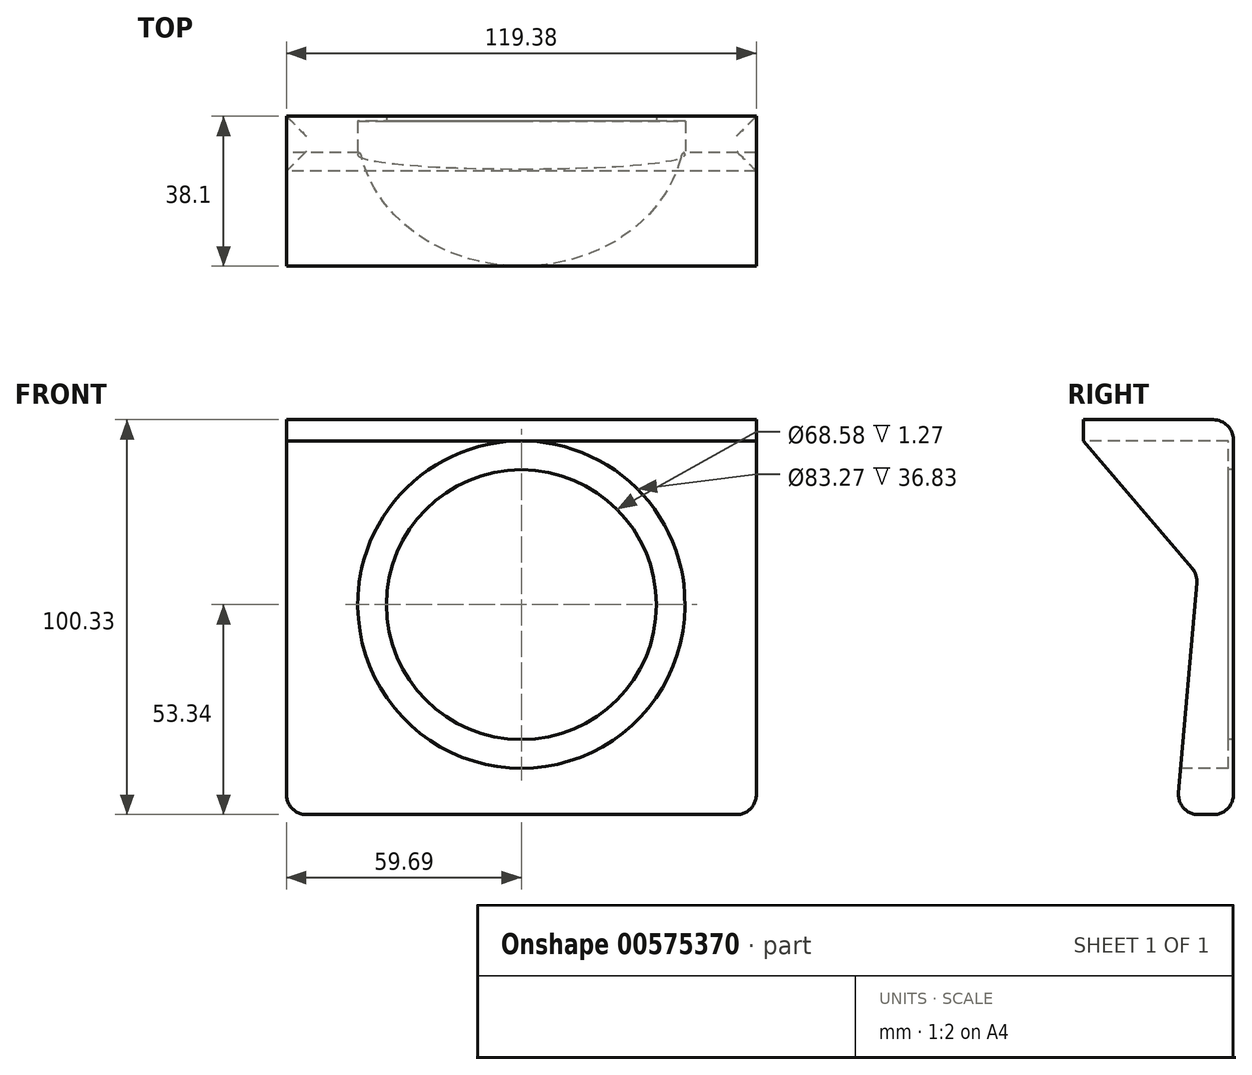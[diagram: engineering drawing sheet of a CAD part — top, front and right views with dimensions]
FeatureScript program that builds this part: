
annotation { "Feature Type Name" : "Feature", "Feature Type Description" : "" }
export const myFeature = defineFeature(function(context is Context, id is Id, definition is map)
    precondition{}
    {
        {
            var Q0;
            Q0=qCreatedBy(makeId("Front.planeOp"),FACE);
            var sketch = newSketch(context, id + "F0", { "sketchPlane" : qUnion([Q0])});
            skCircle(sketch, "E0", {"center": v(0, 0) * mm, "radius": 34.3 * mm});
            skLineSegment(sketch, "E1", {"start": v(-59.7, 47) * mm, "end": v(59.69, 47) * mm});
            skLineSegment(sketch, "E2", {"start": v(-59.7, 47) * mm, "end": v(-59.7, -53.34) * mm});
            skLineSegment(sketch, "E3", {"start": v(59.69, 47) * mm, "end": v(59.7, -53.34) * mm});
            skLineSegment(sketch, "E4", {"start": v(59.7, -53.34) * mm, "end": v(-59.7, -53.34) * mm});
            skSolve(sketch);
        }
        {
            var Q0;
            Q0=makeQuery(id+"F0.imprint","IMPRINT",FACE,{"disambiguationData":[TD([[makeQuery(id+"F0.imprint","IMPRINT",EDGE,{"derivedFrom":sQuery(id+"F0.wireOp",EDGE,"E0")}),-1.0]])]});
            extrude(context, id + "F1", {"entities" : qUnion([Q0]), "oppositeDirection" : true, "depth" : 38.1 * mm, "offsetDistance" : 25.4 * mm});
        }
        {
            var Q0;
            Q0=makeQuery(id+"F1.opExtrude","SWEPT_FACE",FACE,{"disambiguationData":[OSD([sQuery(id+"F0.wireOp",EDGE,"E3")])]});
            var sketch = newSketch(context, id + "F2", { "sketchPlane" : qUnion([Q0])});
            skSolve(sketch);
        }
        {
            var Q0;
            {var subQ0=sQuery(id+"F0.wireOp",EDGE,"E3");Q0=makeQuery(id+"F2.imprint","IMPRINT",FACE,{"disambiguationData":[TD([[makeQuery(id+"F2.imprint","IMPRINT",EDGE,{"derivedFrom":makeQuery(id+"F1.opExtrude","CAP_EDGE",EDGE,{"disambiguationData":[OSD([subQ0])],"isStart":true})}),1.0]])]});}
            var sketch = newSketch(context, id + "F3", { "sketchPlane" : qUnion([Q0])});
            skLineSegment(sketch, "E5", {"start": v(0, 41.6) * mm, "end": v(28.98, 7.67) * mm});
            skLineSegment(sketch, "E6", {"start": v(28.98, 7.67) * mm, "end": v(23.7, -53.34) * mm});
            skLineSegment(sketch, "E7", {"start": v(23.7, -53.34) * mm, "end": v(0, -53.34) * mm});
            skLineSegment(sketch, "E8", {"start": v(0, -53.34) * mm, "end": v(0, 41.6) * mm});
            skSolve(sketch);
        }
        {
            var Q0;
            Q0=makeQuery(id+"F3.imprint","IMPRINT",FACE,{"disambiguationData":[TD([[makeQuery(id+"F3.imprint","IMPRINT",EDGE,{"derivedFrom":sQuery(id+"F3.wireOp",EDGE,"E5")}),-1.0]])]});
            extrude(context, id + "F4", {"entities" : qUnion([Q0]), "operationType" : NewBodyOperationType.REMOVE, "endBound" : BoundingType.THROUGH_ALL, "oppositeDirection" : true, "depth" : 25.4 * mm, "offsetDistance" : 25.4 * mm});
        }
        {
            var Q0;
            {var subQ0=sQuery(id+"F3.wireOp",EDGE,"E5");var subQ1=sQuery(id+"F3.wireOp",EDGE,"E6");Q0=makeQuery(id+"F4.boolean.opBoolean","COPY",EDGE,{"disambiguationData":[TD([makeQuery(id+"F1.opExtrude","SWEPT_FACE",FACE,{"disambiguationData":[OSD([sQuery(id+"F0.wireOp",EDGE,"E3")])]})])],"derivedFrom":makeQuery(id+"F4.opExtrude","SWEPT_EDGE",EDGE,{"disambiguationData":[OSD([subQ0,subQ1])]})});}
            var Q1;
            {var subQ0=sQuery(id+"F3.wireOp",EDGE,"E5");var subQ1=sQuery(id+"F3.wireOp",EDGE,"E6");Q1=makeQuery(id+"F4.boolean.opBoolean","COPY",EDGE,{"disambiguationData":[TD([makeQuery(id+"F1.opExtrude","SWEPT_FACE",FACE,{"disambiguationData":[OSD([sQuery(id+"F0.wireOp",EDGE,"E2")])]})])],"derivedFrom":makeQuery(id+"F4.opExtrude","SWEPT_EDGE",EDGE,{"disambiguationData":[OSD([subQ0,subQ1])]})});}
            fillet(context, id + "F5", {"entities" : qUnion([Q0, Q1]), "radius" : 5.08 * mm, "tangentPropagation" : true, "allowEdgeOverflow" : false});
        }
        {
            var Q0;
            Q0=makeQuery(id+"F1.opExtrude","CAP_EDGE",EDGE,{"disambiguationData":[OSD([sQuery(id+"F0.wireOp",EDGE,"E4")])],"isStart":false});
            var Q1;
            Q1=makeQuery(id+"F1.opExtrude","SWEPT_FACE",FACE,{"disambiguationData":[OSD([sQuery(id+"F0.wireOp",EDGE,"E4")])]});
            fillet(context, id + "F6", {"entities" : qUnion([Q0, Q1]), "radius" : 5.08 * mm, "tangentPropagation" : true, "allowEdgeOverflow" : false});
        }
        {
            var Q0;
            Q0=makeQuery(id+"F1.opExtrude","CAP_EDGE",EDGE,{"disambiguationData":[OSD([sQuery(id+"F0.wireOp",EDGE,"E1")])],"isStart":false});
            fillet(context, id + "F7", {"entities" : qUnion([Q0]), "radius" : 5.08 * mm, "tangentPropagation" : true, "allowEdgeOverflow" : false});
        }
        {
            var Q0;
            Q0=qCreatedBy(makeId("Front.planeOp"),FACE);
            var sketch = newSketch(context, id + "F8", { "sketchPlane" : qUnion([Q0])});
            skArc(sketch, "E9", {"start": v(41.6, 0) * mm, "mid": v(0, 41.6) * mm, "end": v(-41.6, 0) * mm});
            skCircle(sketch, "E10", {"center": v(0, 0) * mm, "radius": 41.63 * mm});
            skSolve(sketch);
        }
        {
            var Q0;
            Q0 = qSketchRegion(id + "F8", true);
            extrude(context, id + "F9", {"entities" : qUnion([Q0]), "operationType" : NewBodyOperationType.REMOVE, "oppositeDirection" : true, "depth" : 36.83 * mm, "offsetDistance" : 25.4 * mm});
        }
    });
